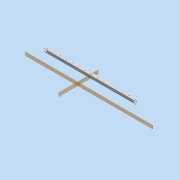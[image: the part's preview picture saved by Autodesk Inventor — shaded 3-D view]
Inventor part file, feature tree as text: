
AUTODESK INVENTOR PART (.ipt)
format: ipt  version: 2015 SP1 (Build 190203100, 203)  size: 147,456 bytes
history: native  units: in
note: dims shown in document units (in); Inventor stores cm internally (conversion verified against a paired STEP export)
features: other x3, plane x2
ambient origin geometry x8: Origin, YZ Plane, XZ Plane, XY Plane, X Axis, Y Axis, Z Axis, Center Point
bodies: Solid1 (feature_tree)
feature tree (5):
  other  "longboard_deck.ipt"
  other  "main_support0::longboard_deck.ipt"
  other  "TaggingFeature1"
  plane  "Work Plane1"
  plane  "Work Plane2"
